# Revit family: Legrand Flush-mounting British standard metal consumer units single phase + neutral
name_source: partatom
category: Equipement électrique
revit_build: Autodesk Revit 2018 (Build: 20170223_1515(x64)
units: mm (PartAtom-declared; Revit-internal decimal feet)

## family parameters
Basée sur le plan de construction = Non
Configuration du panneau = Deux colonnes, circuits au sein
Cote de connecteur circulaire = Utiliser le diamètre
Couper avec des vides une fois chargée = Non
Numéro OmniClass = 23.80.30.11.17
Partagée = Non
Point de calcul de pièce = Non
Titre OmniClass = Distribution Boards and Control Panels
Toujours verticalement = Oui
Type d'élément = Tableau de raccordement

## types (5) — shared parameters
Color = Grey
Fabricant = Legrand
General Conditions of Use = https://export.legrand.com
IP = IP 41
Material = Metallic
Modèle = Flush-mounting British standard
Puissance = 100A
URL = www.legrand.com
depth = 82 mm  [stored 0.269029 ft]
height = 236 mm

## per-type parameters (varying)
| type | 402505 | 402506 | 402507 | 402508 | 402509 | Terminal block E | Terminal block N | number of modules | width |
| Cabinet 402505 | Oui | Non | Non | Non | Non | 4 holes | 4 holes | 2+4 | 190 mm |
| Cabinet 402506 | Non | Oui | Non | Non | Non | 6 holes | 6 holes | 2+6 | 230 mm  [stored 0.754593 ft] |
| Cabinet 402507 | Non | Non | Oui | Non | Non | 8 holes | 8 holes | 2+8 | 260 mm  [stored 0.853018 ft] |
| Cabinet 402508 | Non | Non | Non | Oui | Non | 12 holes | 12 holes | 2+12 | 336 mm  [stored 1.10236 ft] |
| Cabinet 402509 | Non | Non | Non | Non | Oui | 16 holes | 16 holes | 2+14 | 408 mm |

note: [stored X ft] marks values corroborated as IEEE doubles in the binary element streams (Revit-internal decimal feet)
